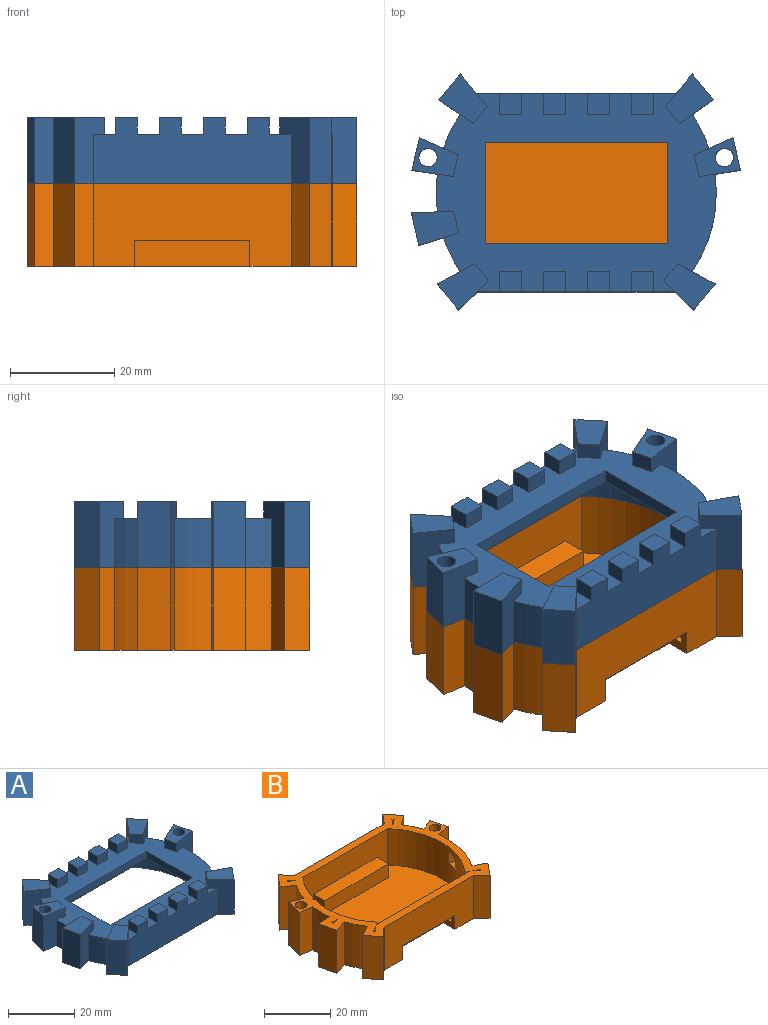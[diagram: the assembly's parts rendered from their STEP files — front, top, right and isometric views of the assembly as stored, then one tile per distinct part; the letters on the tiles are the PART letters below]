
ASSEMBLY  parts=2 mates=1
PART A: 111 faces, bbox 63.3x45.4x12.7 mm
  f0: plane 53.88x38.1mm, normal (0,0,1), area 944.9mm2, adj f2,f3,f4,f6,f7,f8,f10,f11
  f1: plane 63.32x45.36mm, normal (0,0,-1), area 553.4mm2, adj f2,f3,f4,f5,f6,f7,f8,f9
  f2: plane 38.1x12.7mm, normal (0,1,0), area 416.7mm2, adj f0,f1,f3,f31,f91,f92,f94,f95
  f3: cylinder r=26.94mm len=9.53mm, axis (0,0,-1), area 0.7mm2, adj f0,f1,f2,f4
  f4: plane 12.7x6.27mm, normal (0.77,0.64,0), area 73.6mm2, adj f0,f1,f3,f5,f59,f60
  f5: plane 12.7x4.94mm, normal (-0.77,0.64,0), area 81.6mm2, adj f1,f4,f6,f60
  f6: plane 12.7x6.57mm, normal (-0.57,-0.82,0), area 72.9mm2, adj f0,f1,f5,f7,f59,f60
  f7: cylinder r=26.94mm len=9.53mm, axis (0,0,-1), area 69.4mm2, adj f0,f1,f6,f8
  f8: plane 12.7x7.43mm, normal (0.41,0.91,0), area 73.6mm2, adj f0,f1,f7,f9,f61,f62
  f9: plane 12.7x6.25mm, normal (-0.97,0.23,0), area 81.6mm2, adj f1,f8,f10,f62
  f10: plane 12.7x7.94mm, normal (-0.15,-0.99,0), area 72.9mm2, adj f0,f1,f9,f11,f61,f62
  f11: cylinder r=26.94mm len=9.53mm, axis (0,0,-1), area 69.4mm2, adj f0,f1,f10,f12
  f12: plane 12.7x8.13mm, normal (-0.04,1,0), area 73.6mm2, adj f0,f1,f11,f13,f63,f64
  f13: plane 12.7x6.26mm, normal (-0.97,-0.22,0), area 81.6mm2, adj f1,f12,f14,f64
  f14: plane 12.7x7.65mm, normal (0.3,-0.95,0), area 72.9mm2, adj f0,f1,f13,f15,f63,f64
  f15: cylinder r=26.94mm len=9.53mm, axis (0,0,-1), area 69.4mm2, adj f0,f1,f14,f16
  f16: plane 12.7x7.14mm, normal (-0.48,0.88,0), area 73.6mm2, adj f0,f1,f15,f17,f65,f66
  f17: plane 12.7x4.98mm, normal (-0.77,-0.63,0), area 81.6mm2, adj f1,f16,f18,f66
  f18: plane 12.7x5.78mm, normal (0.69,-0.72,0), area 72.9mm2, adj f0,f1,f17,f19,f65,f66
  f19: plane 38.1x12.7mm, normal (0,-1,0), area 416.7mm2, adj f0,f1,f18,f20,f75,f76,f78,f79
  f20: plane 12.7x5.78mm, normal (-0.69,-0.72,0), area 72.9mm2, adj f0,f1,f19,f21,f67,f68
  f21: plane 12.7x4.98mm, normal (0.77,-0.63,0), area 81.6mm2, adj f1,f20,f22,f68
  f22: plane 12.7x7.14mm, normal (0.48,0.88,0), area 73.6mm2, adj f0,f1,f21,f23,f67,f68
  f23: cylinder r=26.94mm len=18.72mm, axis (0,0,-1), area 187.3mm2, adj f0,f1,f22,f24
  f24: plane 12.7x7.94mm, normal (0.15,-0.99,0), area 72.9mm2, adj f0,f1,f23,f25,f69,f70
  f25: plane 12.7x6.25mm, normal (0.97,0.23,0), area 81.6mm2, adj f1,f24,f26,f70
  f26: plane 12.7x7.43mm, normal (-0.41,0.91,0), area 73.6mm2, adj f0,f1,f25,f27,f69,f70
  f27: cylinder r=26.94mm len=9.53mm, axis (0,0,-1), area 69.4mm2, adj f0,f1,f26,f28
  f28: plane 12.7x6.57mm, normal (0.57,-0.82,0), area 72.9mm2, adj f0,f1,f27,f29,f71,f72
  f29: plane 12.7x4.94mm, normal (0.77,0.64,0), area 81.6mm2, adj f1,f28,f30,f72
  f30: plane 12.7x6.27mm, normal (-0.77,0.64,0), area 73.6mm2, adj f0,f1,f29,f31,f71,f72
  f31: cylinder r=26.94mm len=9.53mm, axis (0,0,-1), area 0.7mm2, adj f0,f1,f2,f30
  f32: plane 7.03x2.03mm, normal (0.77,-0.64,0), area 18.5mm2, adj f1,f33,f34,f35
  f33: plane 7.03x0.54mm, normal (-0.77,-0.64,0), area 4.9mm2, adj f1,f32,f34,f35
  f34: plane 7.03x2.13mm, normal (-0.57,0.82,0), area 18.2mm2, adj f1,f32,f33,f35
  f35: plane 2.13x2.03mm, normal (0,0,-1), area 0.9mm2, adj f32,f33,f34
  f36: plane 7.03x2.47mm, normal (-0.3,0.95,0), area 18.2mm2, adj f1,f37,f38,f39
  f37: plane 7.03x0.68mm, normal (0.97,0.22,0), area 4.9mm2, adj f1,f36,f38,f39
  f38: plane 7.03x2.63mm, normal (0.04,-1,0), area 18.5mm2, adj f1,f36,f37,f39
  f39: plane 2.63x0.79mm, normal (0,0,-1), area 0.9mm2, adj f36,f37,f38
  f40: plane 7.03x2.13mm, normal (0.57,0.82,0), area 18.2mm2, adj f1,f41,f42,f43
  f41: plane 7.03x0.54mm, normal (0.77,-0.64,0), area 4.9mm2, adj f1,f40,f42,f43
  f42: plane 7.03x2.03mm, normal (-0.77,-0.64,0), area 18.5mm2, adj f1,f40,f41,f43
  f43: plane 2.13x2.03mm, normal (0,0,-1), area 0.9mm2, adj f40,f41,f42
  f44: cylinder r=24.44mm len=32.47mm, axis (0,0,-1), area 249.6mm2, adj f1,f48,f49,f50
  f45: plane 39.38x7.03mm, normal (0,1,0), area 276.6mm2, adj f1,f46,f49,f50
  f46: plane 7.03x1.15mm, normal (0.48,-0.88,0), area 9.2mm2, adj f1,f45,f47,f49
  f47: cylinder r=24.44mm len=32.47mm, axis (0,0,-1), area 249.6mm2, adj f1,f46,f48,f49
  f48: plane 35.97x7.03mm, normal (0,-1,0), area 252.7mm2, adj f1,f44,f47,f49
  f49: plane 48.88x33.1mm, normal (0,0,-1), area 802.6mm2, adj f44,f45,f46,f47,f48,f50,f107,f108
  f50: plane 7.03x1.15mm, normal (-0.48,-0.88,0), area 9.2mm2, adj f1,f44,f45,f49
  f51: plane 7.03x1.87mm, normal (0.69,0.72,0), area 18.2mm2, adj f1,f52,f53,f54
  f52: plane 7.03x0.54mm, normal (-0.77,0.63,0), area 4.9mm2, adj f1,f51,f53,f54
  f53: plane 7.03x2.31mm, normal (-0.48,-0.88,0), area 18.5mm2, adj f1,f51,f52,f54
  f54: plane 2.31x1.8mm, normal (0,0,-1), area 0.9mm2, adj f51,f52,f53
  f55: plane 7.03x1.87mm, normal (-0.69,0.72,0), area 18.2mm2, adj f1,f56,f57,f58
  f56: plane 7.03x0.54mm, normal (0.77,0.63,0), area 4.9mm2, adj f1,f55,f57,f58
  f57: plane 2.31x1.8mm, normal (0,0,-1), area 0.9mm2, adj f55,f56,f58
  f58: plane 7.03x2.31mm, normal (0.48,-0.88,0), area 18.5mm2, adj f1,f55,f56,f57
  f59: plane 3.28x3.18mm, normal (0.77,-0.64,0), area 13.5mm2, adj f0,f4,f6,f60
  f60: plane 9.55x9.3mm, normal (0,0,1), area 42.8mm2, adj f4,f5,f6,f59
  f61: plane 4.15x3.18mm, normal (0.97,-0.23,0), area 13.5mm2, adj f0,f8,f10,f62
  f62: plane 8.93x7.46mm, normal (0,0,1), area 33.1mm2, adj f8,f9,f10,f61,f73
  f63: plane 4.16x3.18mm, normal (0.97,0.22,0), area 13.5mm2, adj f0,f12,f14,f64
  f64: plane 9.08x6.59mm, normal (0,0,1), area 42.8mm2, adj f12,f13,f14,f63
  f65: plane 3.3x3.18mm, normal (0.77,0.63,0), area 13.5mm2, adj f0,f16,f18,f66
  f66: plane 9.84x8.88mm, normal (0,0,1), area 42.8mm2, adj f16,f17,f18,f65
  f67: plane 3.3x3.18mm, normal (-0.77,0.63,0), area 13.5mm2, adj f0,f20,f22,f68
  f68: plane 9.84x8.88mm, normal (0,0,1), area 42.8mm2, adj f20,f21,f22,f67
  f69: plane 4.15x3.18mm, normal (-0.97,-0.23,0), area 13.5mm2, adj f0,f24,f26,f70
  f70: plane 8.93x7.46mm, normal (0,0,1), area 33.1mm2, adj f24,f25,f26,f69,f74
  f71: plane 3.28x3.18mm, normal (-0.77,-0.64,0), area 13.5mm2, adj f0,f28,f30,f72
  f72: plane 9.55x9.3mm, normal (0,0,1), area 42.8mm2, adj f28,f29,f30,f71
  f73: cylinder r=1.75mm len=12.7mm, axis (0,0,1), area 139.9mm2, adj f1,f62
  f74: cylinder r=1.75mm len=12.7mm, axis (0,0,1), area 139.9mm2, adj f1,f70
  f75: plane 4x3.18mm, normal (-1,0,0), area 12.7mm2, adj f0,f19,f77,f78
  f76: plane 4x3.18mm, normal (1,0,0), area 12.7mm2, adj f0,f19,f77,f78
  f77: plane 4.23x3.18mm, normal (0,1,0), area 13.4mm2, adj f0,f75,f76,f78
  f78: plane 4.23x4mm, normal (0,0,1), area 16.9mm2, adj f19,f75,f76,f77
  f79: plane 4x3.18mm, normal (-1,0,0), area 12.7mm2, adj f0,f19,f81,f82
  f80: plane 4x3.18mm, normal (1,0,0), area 12.7mm2, adj f0,f19,f81,f82
  f81: plane 4.23x3.18mm, normal (0,1,0), area 13.4mm2, adj f0,f79,f80,f82
  f82: plane 4.23x4mm, normal (0,0,1), area 16.9mm2, adj f19,f79,f80,f81
  f83: plane 4x3.18mm, normal (-1,0,0), area 12.7mm2, adj f0,f19,f85,f86
  f84: plane 4x3.18mm, normal (1,0,0), area 12.7mm2, adj f0,f19,f85,f86
  f85: plane 4.23x3.18mm, normal (0,1,0), area 13.4mm2, adj f0,f83,f84,f86
  f86: plane 4.23x4mm, normal (0,0,1), area 16.9mm2, adj f19,f83,f84,f85
  f87: plane 4x3.18mm, normal (-1,0,0), area 12.7mm2, adj f0,f19,f89,f90
  f88: plane 4x3.18mm, normal (1,0,0), area 12.7mm2, adj f0,f19,f89,f90
  f89: plane 4.23x3.18mm, normal (0,1,0), area 13.4mm2, adj f0,f87,f88,f90
  f90: plane 4.23x4mm, normal (0,0,1), area 16.9mm2, adj f19,f87,f88,f89
  f91: plane 4x3.18mm, normal (1,0,0), area 12.7mm2, adj f0,f2,f93,f94
  f92: plane 4x3.18mm, normal (-1,0,0), area 12.7mm2, adj f0,f2,f93,f94
  f93: plane 4.23x3.18mm, normal (0,-1,0), area 13.4mm2, adj f0,f91,f92,f94
  f94: plane 4.23x4mm, normal (0,0,1), area 16.9mm2, adj f2,f91,f92,f93
  f95: plane 4x3.18mm, normal (1,0,0), area 12.7mm2, adj f0,f2,f97,f98
  f96: plane 4x3.18mm, normal (-1,0,0), area 12.7mm2, adj f0,f2,f97,f98
  f97: plane 4.23x3.18mm, normal (0,-1,0), area 13.4mm2, adj f0,f95,f96,f98
  f98: plane 4.23x4mm, normal (0,0,1), area 16.9mm2, adj f2,f95,f96,f97
  f99: plane 4x3.18mm, normal (1,0,0), area 12.7mm2, adj f0,f2,f101,f102
  f100: plane 4x3.18mm, normal (-1,0,0), area 12.7mm2, adj f0,f2,f101,f102
  f101: plane 4.23x3.18mm, normal (0,-1,0), area 13.4mm2, adj f0,f99,f100,f102
  f102: plane 4.23x4mm, normal (0,0,1), area 16.9mm2, adj f2,f99,f100,f101
  f103: plane 4x3.18mm, normal (1,0,0), area 12.7mm2, adj f0,f2,f105,f106
  f104: plane 4x3.18mm, normal (-1,0,0), area 12.7mm2, adj f0,f2,f105,f106
  f105: plane 4.23x3.18mm, normal (0,-1,0), area 13.4mm2, adj f0,f103,f104,f106
  f106: plane 4.23x4mm, normal (0,0,1), area 16.9mm2, adj f2,f103,f104,f105
  f107: plane 35x2.5mm, normal (0,-1,0), area 87.5mm2, adj f0,f49,f108,f110
  f108: plane 19.5x2.5mm, normal (1,0,0), area 48.8mm2, adj f0,f49,f107,f109
  f109: plane 35x2.5mm, normal (0,1,0), area 87.5mm2, adj f0,f49,f108,f110
  f110: plane 19.5x2.5mm, normal (-1,0,0), area 48.8mm2, adj f0,f49,f107,f109
PART B: 89 faces, bbox 63.3x45.4x15.9 mm
  f0: cylinder r=26.94mm len=18.72mm, axis (0,0,-1), area 296.1mm2, adj f2,f3,f24,f25,f85,f86,f87,f88
  f1: cylinder r=24.44mm len=32.47mm, axis (0,0,-1), area 459.1mm2, adj f2,f61,f63,f65,f85,f86,f87,f88
  f2: plane 63.32x45.36mm, normal (0,0,1), area 553.4mm2, adj f0,f1,f4,f5,f6,f7,f8,f9
  f3: plane 63.32x45.36mm, normal (0,0,-1), area 1827.4mm2, adj f0,f4,f5,f6,f7,f8,f9,f10
  f4: plane 38.1x15.88mm, normal (0,-1,0), area 493.7mm2, adj f2,f3,f21,f22,f37,f39,f40
  f5: plane 38.1x15.88mm, normal (0,1,0), area 493.7mm2, adj f2,f3,f6,f32,f33,f35,f36
  f6: cylinder r=26.94mm len=15.88mm, axis (0,0,-1), area 1.1mm2, adj f2,f3,f5,f7
  f7: plane 15.88x3.86mm, normal (0.77,0.64,0), area 79.6mm2, adj f2,f3,f6,f8
  f8: plane 15.88x4.94mm, normal (-0.77,0.64,0), area 102mm2, adj f2,f3,f7,f9
  f9: plane 15.88x4.07mm, normal (-0.57,-0.82,0), area 79mm2, adj f2,f3,f8,f10
  f10: cylinder r=26.94mm len=15.88mm, axis (0,0,-1), area 115.6mm2, adj f2,f3,f9,f11
  f11: plane 15.88x4.58mm, normal (0.41,0.91,0), area 79.6mm2, adj f2,f3,f10,f12
  f12: plane 15.88x6.25mm, normal (-0.97,0.23,0), area 102mm2, adj f2,f3,f11,f13
  f13: plane 15.88x4.92mm, normal (-0.15,-0.99,0), area 79mm2, adj f2,f3,f12,f14
  f14: cylinder r=26.94mm len=15.88mm, axis (0,0,-1), area 115.6mm2, adj f2,f3,f13,f15
  f15: plane 15.88x5.01mm, normal (-0.04,1,0), area 79.6mm2, adj f2,f3,f14,f16
  f16: plane 15.88x6.26mm, normal (-0.97,-0.22,0), area 102mm2, adj f2,f3,f15,f17
  f17: plane 15.88x4.74mm, normal (0.3,-0.95,0), area 79mm2, adj f2,f3,f16,f18
  f18: cylinder r=26.94mm len=15.88mm, axis (0,0,-1), area 115.6mm2, adj f2,f3,f17,f19
  f19: plane 15.88x4.4mm, normal (-0.48,0.88,0), area 79.6mm2, adj f2,f3,f18,f20
  f20: plane 15.88x4.98mm, normal (-0.77,-0.63,0), area 102mm2, adj f2,f3,f19,f21
  f21: plane 15.88x3.58mm, normal (0.69,-0.72,0), area 79mm2, adj f2,f3,f4,f20
  f22: plane 15.88x3.58mm, normal (-0.69,-0.72,0), area 79mm2, adj f2,f3,f4,f23
  f23: plane 15.88x4.98mm, normal (0.77,-0.63,0), area 102mm2, adj f2,f3,f22,f24
  f24: plane 15.88x4.4mm, normal (0.48,0.88,0), area 79.6mm2, adj f0,f2,f3,f23
  f25: plane 15.88x4.92mm, normal (0.15,-0.99,0), area 79mm2, adj f0,f2,f3,f26
  f26: plane 15.88x6.25mm, normal (0.97,0.23,0), area 102mm2, adj f2,f3,f25,f27
  f27: plane 15.88x4.58mm, normal (-0.41,0.91,0), area 79.6mm2, adj f2,f3,f26,f28
  f28: cylinder r=26.94mm len=15.88mm, axis (0,0,-1), area 115.6mm2, adj f2,f3,f27,f29
  f29: plane 15.88x4.07mm, normal (0.57,-0.82,0), area 79mm2, adj f2,f3,f28,f30
  f30: plane 15.88x4.94mm, normal (0.77,0.64,0), area 102mm2, adj f2,f3,f29,f31
  f31: plane 15.88x3.86mm, normal (-0.77,0.64,0), area 79.6mm2, adj f2,f3,f30,f32
  f32: cylinder r=26.94mm len=15.88mm, axis (0,0,-1), area 1.1mm2, adj f2,f3,f5,f31
  f33: plane 5x4.85mm, normal (-1,0,0), area 22.4mm2, adj f3,f5,f34,f36,f83
  f34: plane 22.22x5mm, normal (0,1,0), area 111.1mm2, adj f3,f33,f35,f36
  f35: plane 5x4.85mm, normal (1,0,0), area 22.4mm2, adj f3,f5,f34,f36,f79
  f36: plane 22.22x4.85mm, normal (0,0,-1), area 107.8mm2, adj f5,f33,f34,f35
  f37: plane 5x4.85mm, normal (1,0,0), area 22.4mm2, adj f3,f4,f38,f40,f77
  f38: plane 22.22x5mm, normal (0,-1,0), area 111.1mm2, adj f3,f37,f39,f40
  f39: plane 5x4.85mm, normal (-1,0,0), area 22.4mm2, adj f3,f4,f38,f40,f81
  f40: plane 22.22x4.85mm, normal (0,0,-1), area 107.8mm2, adj f4,f37,f38,f39
  f41: plane 13.38x2.13mm, normal (0.57,0.82,0), area 34.7mm2, adj f2,f42,f43,f44
  f42: plane 13.38x0.54mm, normal (0.77,-0.64,0), area 9.3mm2, adj f2,f41,f43,f44
  f43: plane 13.38x2.03mm, normal (-0.77,-0.64,0), area 35.2mm2, adj f2,f41,f42,f44
  f44: plane 2.13x2.03mm, normal (0,0,1), area 0.9mm2, adj f41,f42,f43
  f45: plane 13.38x2.47mm, normal (-0.3,0.95,0), area 34.7mm2, adj f2,f46,f47,f48
  f46: plane 13.38x0.68mm, normal (0.97,0.22,0), area 9.3mm2, adj f2,f45,f47,f48
  f47: plane 13.38x2.63mm, normal (0.04,-1,0), area 35.2mm2, adj f2,f45,f46,f48
  f48: plane 2.63x0.79mm, normal (0,0,1), area 0.9mm2, adj f45,f46,f47
  f49: plane 13.38x2.03mm, normal (0.77,-0.64,0), area 35.2mm2, adj f2,f50,f51,f52
  f50: plane 13.38x0.54mm, normal (-0.77,-0.64,0), area 9.3mm2, adj f2,f49,f51,f52
  f51: plane 13.38x2.13mm, normal (-0.57,0.82,0), area 34.7mm2, adj f2,f49,f50,f52
  f52: plane 2.13x2.03mm, normal (0,0,1), area 0.9mm2, adj f49,f50,f51
  f53: plane 27.22x4.85mm, normal (0,0,1), area 132mm2, adj f54,f55,f56,f64
  f54: plane 5x4.85mm, normal (1,0,0), area 24.2mm2, adj f53,f55,f64,f65
  f55: plane 27.22x5mm, normal (0,1,0), area 136.1mm2, adj f53,f54,f56,f65
  f56: plane 5x4.85mm, normal (-1,0,0), area 24.2mm2, adj f53,f55,f64,f65
  f57: plane 27.22x4.85mm, normal (0,0,1), area 132mm2, adj f58,f59,f60,f63
  f58: plane 5x4.85mm, normal (-1,0,0), area 24.2mm2, adj f57,f59,f63,f65
  f59: plane 27.22x5mm, normal (0,-1,0), area 136.1mm2, adj f57,f58,f60,f65
  f60: plane 5x4.85mm, normal (1,0,0), area 24.2mm2, adj f57,f59,f63,f65
  f61: plane 13.38x1.15mm, normal (-0.48,-0.88,0), area 17.5mm2, adj f1,f2,f64,f65
  f62: cylinder r=24.44mm len=32.47mm, axis (0,0,-1), area 475.1mm2, adj f2,f63,f65,f66
  f63: plane 35.97x13.38mm, normal (0,-1,0), area 345mm2, adj f1,f2,f57,f58,f60,f62,f65
  f64: plane 39.38x13.38mm, normal (0,1,0), area 390.6mm2, adj f2,f53,f54,f56,f61,f65,f66
  f65: plane 48.88x33.1mm, normal (0,0,1), area 1221mm2, adj f1,f54,f55,f56,f58,f59,f60,f61
  f66: plane 13.38x1.15mm, normal (0.48,-0.88,0), area 17.5mm2, adj f2,f62,f64,f65
  f67: plane 2.31x1.8mm, normal (0,0,1), area 0.9mm2, adj f68,f69,f70
  f68: plane 13.38x2.31mm, normal (0.48,-0.88,0), area 35.2mm2, adj f2,f67,f69,f70
  f69: plane 13.38x0.54mm, normal (0.77,0.63,0), area 9.3mm2, adj f2,f67,f68,f70
  f70: plane 13.38x1.87mm, normal (-0.69,0.72,0), area 34.7mm2, adj f2,f67,f68,f69
  f71: plane 13.38x0.54mm, normal (-0.77,0.63,0), area 9.3mm2, adj f2,f72,f73,f74
  f72: plane 13.38x1.87mm, normal (0.69,0.72,0), area 34.7mm2, adj f2,f71,f73,f74
  f73: plane 2.31x1.8mm, normal (0,0,1), area 0.9mm2, adj f71,f72,f74
  f74: plane 13.38x2.31mm, normal (-0.48,-0.88,0), area 35.2mm2, adj f2,f71,f72,f73
  f75: cylinder r=1.75mm len=15.88mm, axis (0,0,1), area 174.8mm2, adj f2,f3
  f76: cylinder r=1.75mm len=15.88mm, axis (0,0,1), area 174.8mm2, adj f2,f3
  f77: cylinder r=0.76mm len=1.52mm, axis (1,0,0), area 7.2mm2, adj f37,f78
  f78: plane 1.52x1.52mm, normal (1,0,0), area 1.8mm2, adj f77
  f79: cylinder r=0.76mm len=1.52mm, axis (1,0,0), area 7.2mm2, adj f35,f80
  f80: plane 1.52x1.52mm, normal (1,0,0), area 1.8mm2, adj f79
  f81: cylinder r=0.76mm len=1.52mm, axis (-1,0,0), area 7.2mm2, adj f39,f82
  f82: plane 1.52x1.52mm, normal (-1,0,0), area 1.8mm2, adj f81
  f83: cylinder r=0.76mm len=1.52mm, axis (-1,0,0), area 7.2mm2, adj f33,f84
  f84: plane 1.52x1.52mm, normal (-1,0,0), area 1.8mm2, adj f83
  f85: plane 4x2.45mm, normal (-0.22,-0.98,0), area 10mm2, adj f0,f1,f86,f88
  f86: plane 4.46x3.33mm, normal (0,0,1), area 10mm2, adj f0,f1,f85,f87
  f87: plane 4x2.45mm, normal (0.22,0.98,0), area 10mm2, adj f0,f1,f86,f88
  f88: plane 4.46x3.33mm, normal (0,0,-1), area 10mm2, adj f0,f1,f85,f87
PLACE A t=(1.5,15.27,25.2)mm
PLACE B t=(1.5,15.27,9.32)mm
MATE planar B.f2 <-> A.f1  axis (0,0,1) through (20.55,-3.78,25.2)mm
